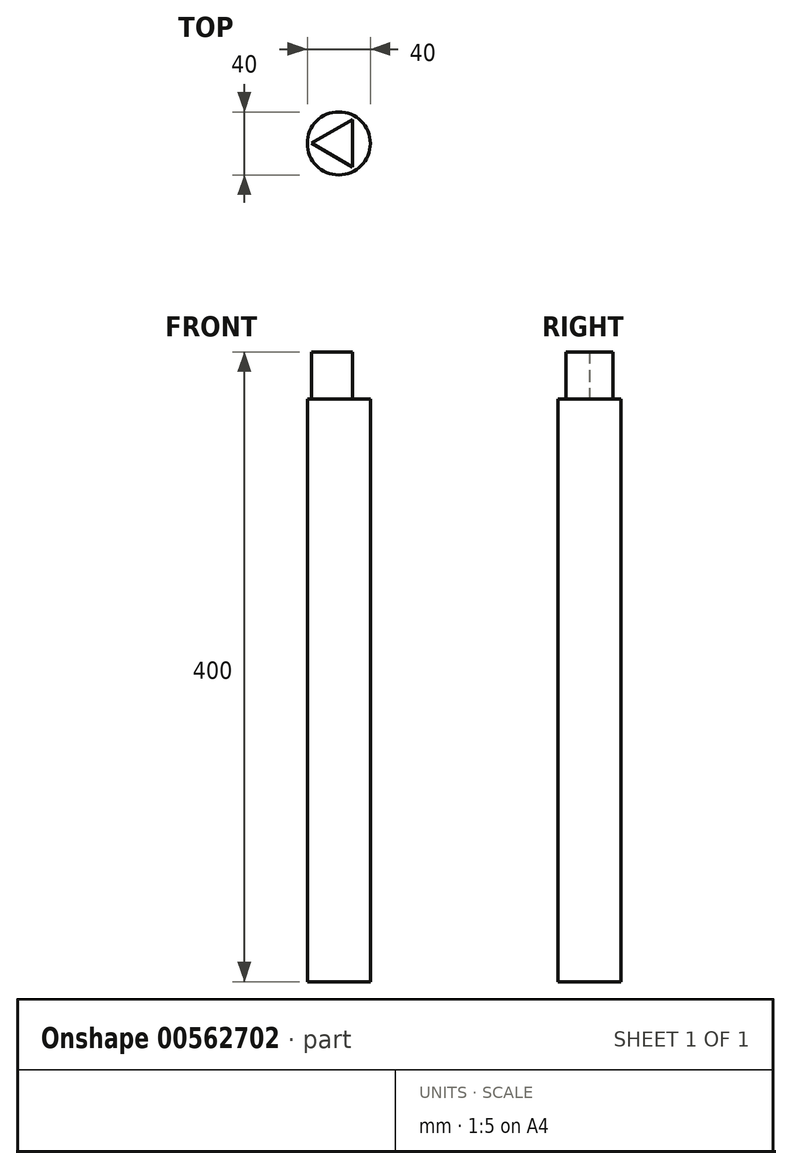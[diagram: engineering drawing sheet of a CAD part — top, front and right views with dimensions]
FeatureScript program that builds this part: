
annotation { "Feature Type Name" : "Feature", "Feature Type Description" : "" }
export const myFeature = defineFeature(function(context is Context, id is Id, definition is map)
    precondition{}
    {
        {
            var Q0;
            Q0=qCreatedBy(makeId("Top.planeOp"),FACE);
            var sketch = newSketch(context, id + "F0", { "sketchPlane" : qUnion([Q0])});
            skCircle(sketch, "E0", {"center": v(0, 0) * mm, "radius": 20 * mm});
            skSolve(sketch);
        }
        {
            var Q0;
            Q0=makeQuery(id+"F0.imprint","IMPRINT",FACE,{"disambiguationData":[TD([[makeQuery(id+"F0.imprint","IMPRINT",EDGE,{"derivedFrom":sQuery(id+"F0.wireOp",EDGE,"E0")}),1.0]])]});
            extrude(context, id + "F1", {"entities" : qUnion([Q0]), "depth" : 370 * mm, "offsetDistance" : 25.4 * mm});
        }
        {
            var Q0;
            Q0=makeQuery(id+"F1.opExtrude","CAP_FACE",FACE,{"disambiguationData":[OSD([sQuery(id+"F0.wireOp",EDGE,"E0")])],"isStart":false});
            var sketch = newSketch(context, id + "F2", { "sketchPlane" : qUnion([Q0])});
            skCircle(sketch, "E1.cCircle", {"center": v(0, 0) * mm, "radius": 17.32 * mm, "construction": true});
            skLineSegment(sketch, "E1.0", {"start": v(8.6, -15.03) * mm, "end": v(-17.32, 0.06) * mm});
            skLineSegment(sketch, "E1.1", {"start": v(-17.32, 0.06) * mm, "end": v(8.71, 14.97) * mm});
            skLineSegment(sketch, "E1.2", {"start": v(8.71, 14.97) * mm, "end": v(8.6, -15.03) * mm});
            skSolve(sketch);
        }
        {
            var Q0;
            Q0 = qSketchRegion(id + "F2", true);
            extrude(context, id + "F3", {"entities" : qUnion([Q0]), "operationType" : NewBodyOperationType.ADD, "depth" : 30 * mm, "offsetDistance" : 25.4 * mm});
        }
    });
